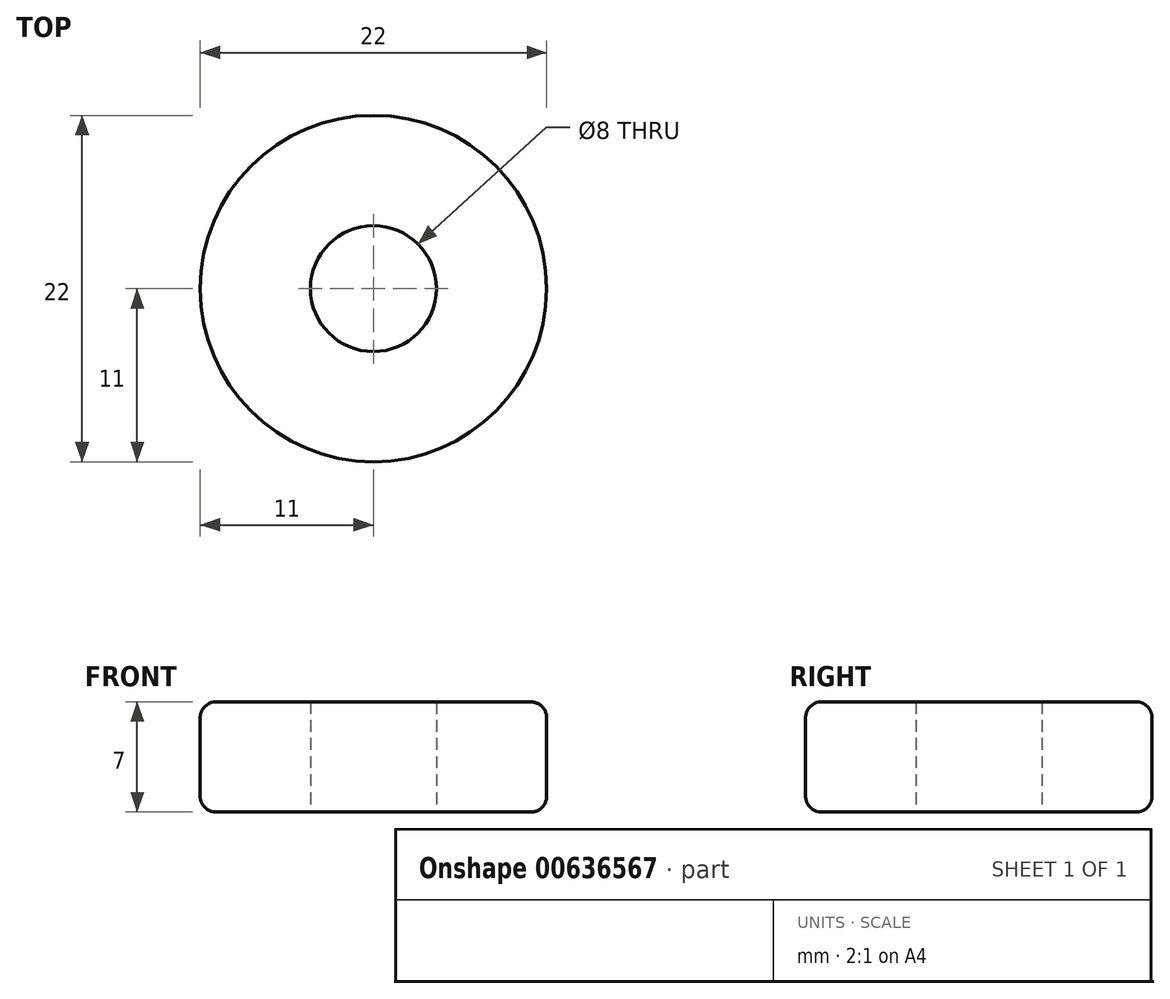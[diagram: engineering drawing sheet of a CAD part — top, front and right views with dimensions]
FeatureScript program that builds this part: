
annotation { "Feature Type Name" : "Feature", "Feature Type Description" : "" }
export const myFeature = defineFeature(function(context is Context, id is Id, definition is map)
    precondition{}
    {
        {
            var Q0;
            Q0=qCreatedBy(makeId("Top.planeOp"),FACE);
            var sketch = newSketch(context, id + "F0", { "sketchPlane" : qUnion([Q0])});
            skCircle(sketch, "E0", {"center": v(0, 0) * mm, "radius": 11 * mm});
            skCircle(sketch, "E1", {"center": v(0, 0) * mm, "radius": 4 * mm});
            skSolve(sketch);
        }
        {
            var Q0;
            Q0 = qSketchRegion(id + "F0", true);
            extrude(context, id + "F1", {"entities" : qUnion([Q0]), "depth" : 7 * mm, "offsetDistance" : 25 * mm});
        }
        {
            var Q0;
            Q0=makeQuery(id+"F1.opExtrude","CAP_EDGE",EDGE,{"disambiguationData":[OSD([sQuery(id+"F0.wireOp",EDGE,"E0")])],"isStart":true});
            var Q1;
            Q1=makeQuery(id+"F1.opExtrude","CAP_EDGE",EDGE,{"disambiguationData":[OSD([sQuery(id+"F0.wireOp",EDGE,"E0")])],"isStart":false});
            fillet(context, id + "F2", {"entities" : qUnion([Q0, Q1]), "radius" : 1 * mm, "tangentPropagation" : true, "allowEdgeOverflow" : false});
        }
    });
